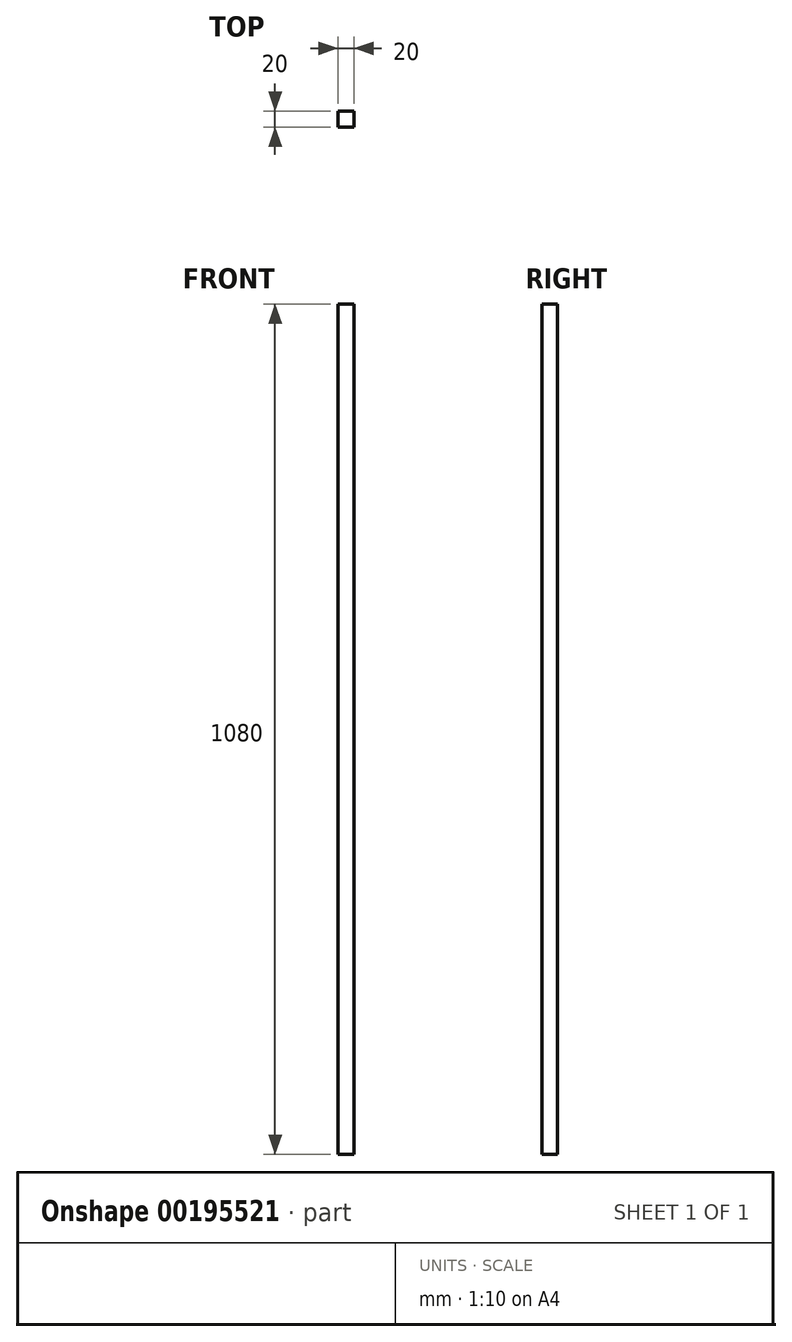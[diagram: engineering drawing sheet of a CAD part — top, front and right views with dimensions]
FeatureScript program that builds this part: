
annotation { "Feature Type Name" : "Feature", "Feature Type Description" : "" }
export const myFeature = defineFeature(function(context is Context, id is Id, definition is map)
    precondition{}
    {
        {
            var Q0;
            Q0=qCreatedBy(makeId("Top.planeOp"),FACE);
            var sketch = newSketch(context, id + "F0", { "sketchPlane" : qUnion([Q0])});
            skLineSegment(sketch, "E0.bottom", {"start": v(-70.8, -20) * mm, "end": v(-50.8, -20) * mm});
            skLineSegment(sketch, "E0.top", {"start": v(-70.8, 0) * mm, "end": v(-50.8, 0) * mm});
            skLineSegment(sketch, "E0.left", {"start": v(-70.8, -20) * mm, "end": v(-70.8, 0) * mm});
            skLineSegment(sketch, "E0.right", {"start": v(-50.8, -20) * mm, "end": v(-50.8, 0) * mm});
            skSolve(sketch);
        }
        {
            var Q0;
            Q0=makeQuery(id+"F0.imprint","IMPRINT",FACE,{"disambiguationData":[TD([[makeQuery(id+"F0.imprint","IMPRINT",EDGE,{"derivedFrom":sQuery(id+"F0.wireOp",EDGE,"E0.bottom")}),1.0]])]});
            extrude(context, id + "F1", {"entities" : qUnion([Q0]), "depth" : 1080 * mm});
        }
    });
